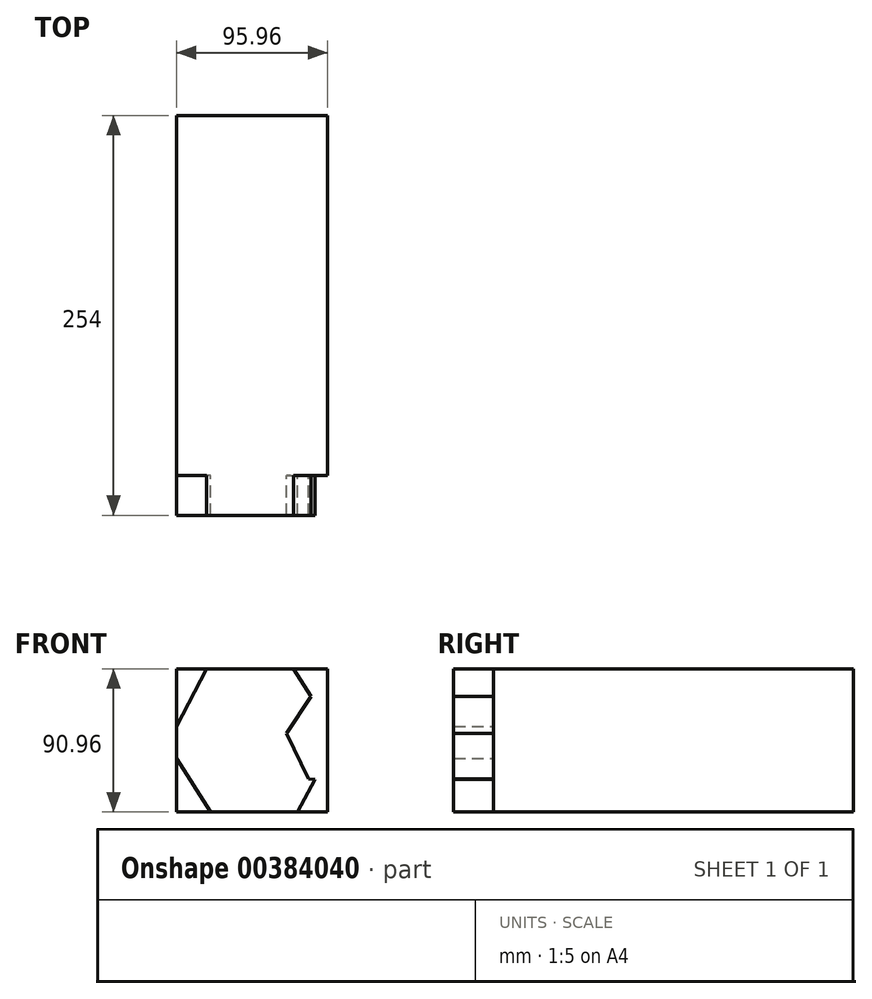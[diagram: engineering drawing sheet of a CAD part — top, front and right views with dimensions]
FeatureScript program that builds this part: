
annotation { "Feature Type Name" : "Feature", "Feature Type Description" : "" }
export const myFeature = defineFeature(function(context is Context, id is Id, definition is map)
    precondition{}
    {
        {
            var Q0;
            Q0=qCreatedBy(makeId("Front.planeOp"),FACE);
            var sketch = newSketch(context, id + "F0", { "sketchPlane" : qUnion([Q0])});
            skLineSegment(sketch, "E0.bottom", {"start": v(47.98, 45.48) * mm, "end": v(-47.98, 45.48) * mm});
            skLineSegment(sketch, "E0.top", {"start": v(47.98, -45.48) * mm, "end": v(-47.98, -45.48) * mm});
            skLineSegment(sketch, "E0.left", {"start": v(47.98, 45.48) * mm, "end": v(47.98, -45.48) * mm});
            skLineSegment(sketch, "E0.right", {"start": v(-47.98, 45.48) * mm, "end": v(-47.98, -45.48) * mm});
            skPoint(sketch, "E0.middle", {"position": v(0, 0) * mm});
            skSolve(sketch);
        }
        {
            var Q0;
            Q0=makeQuery(id+"F0.imprint","IMPRINT",FACE,{"disambiguationData":[TD([[makeQuery(id+"F0.imprint","IMPRINT",EDGE,{"derivedFrom":sQuery(id+"F0.wireOp",EDGE,"E0.bottom")}),1.0]])]});
            extrude(context, id + "F1", {"entities" : qUnion([Q0]), "endBound" : BoundingType.SYMMETRIC, "depth" : 228.6 * mm});
        }
        {
            var Q0;
            Q0=makeQuery(id+"F1.opExtrude","CAP_FACE",FACE,{"disambiguationData":[OSD([sQuery(id+"F0.wireOp",EDGE,"E0.bottom"),sQuery(id+"F0.wireOp",EDGE,"E0.top"),sQuery(id+"F0.wireOp",EDGE,"E0.left"),sQuery(id+"F0.wireOp",EDGE,"E0.right")])],"isStart":false});
            var sketch = newSketch(context, id + "F2", { "sketchPlane" : qUnion([Q0])});
            skCircle(sketch, "E1.cCircle", {"center": v(0, 0) * mm, "radius": 53.9 * mm, "construction": true});
            skLineSegment(sketch, "E1.0", {"start": v(28.93, -45.48) * mm, "end": v(-24.92, -47.79) * mm});
            skLineSegment(sketch, "E1.1", {"start": v(-24.92, -47.79) * mm, "end": v(-53.85, -2.31) * mm});
            skLineSegment(sketch, "E1.2", {"start": v(-53.85, -2.31) * mm, "end": v(-28.93, 45.48) * mm});
            skLineSegment(sketch, "E1.3", {"start": v(-28.93, 45.48) * mm, "end": v(24.92, 47.79) * mm});
            skLineSegment(sketch, "E1.4", {"start": v(24.92, 47.79) * mm, "end": v(53.85, 2.31) * mm});
            skLineSegment(sketch, "E1.5", {"start": v(53.85, 2.31) * mm, "end": v(28.93, -45.48) * mm});
            skCircle(sketch, "E2.cCircle", {"center": v(53.85, 2.31) * mm, "radius": 32.22 * mm, "construction": true});
            skLineSegment(sketch, "E2.0", {"start": v(85.98, 0) * mm, "end": v(67.91, -26.67) * mm});
            skLineSegment(sketch, "E2.1", {"start": v(67.91, -26.67) * mm, "end": v(35.78, -24.36) * mm});
            skLineSegment(sketch, "E2.2", {"start": v(35.78, -24.36) * mm, "end": v(21.72, 4.62) * mm});
            skLineSegment(sketch, "E2.3", {"start": v(21.72, 4.62) * mm, "end": v(39.78, 31.3) * mm});
            skLineSegment(sketch, "E2.4", {"start": v(39.78, 31.3) * mm, "end": v(71.92, 28.98) * mm});
            skLineSegment(sketch, "E2.5", {"start": v(71.92, 28.98) * mm, "end": v(85.98, 0) * mm});
            skSolve(sketch);
        }
        {
            var Q0;
            {var subQ14=sQuery(id+"F2.wireOp",EDGE,"E2.2");Q0=makeQuery(id+"F2.imprint","IMPRINT",FACE,{"disambiguationData":[TD([[makeQuery(id+"F2.imprint","IMPRINT",EDGE,{"derivedFrom":subQ14}),1.0]])]});}
            extrude(context, id + "F3", {"entities" : qUnion([Q0]), "operationType" : NewBodyOperationType.ADD, "depth" : 25.4 * mm});
        }
    });
